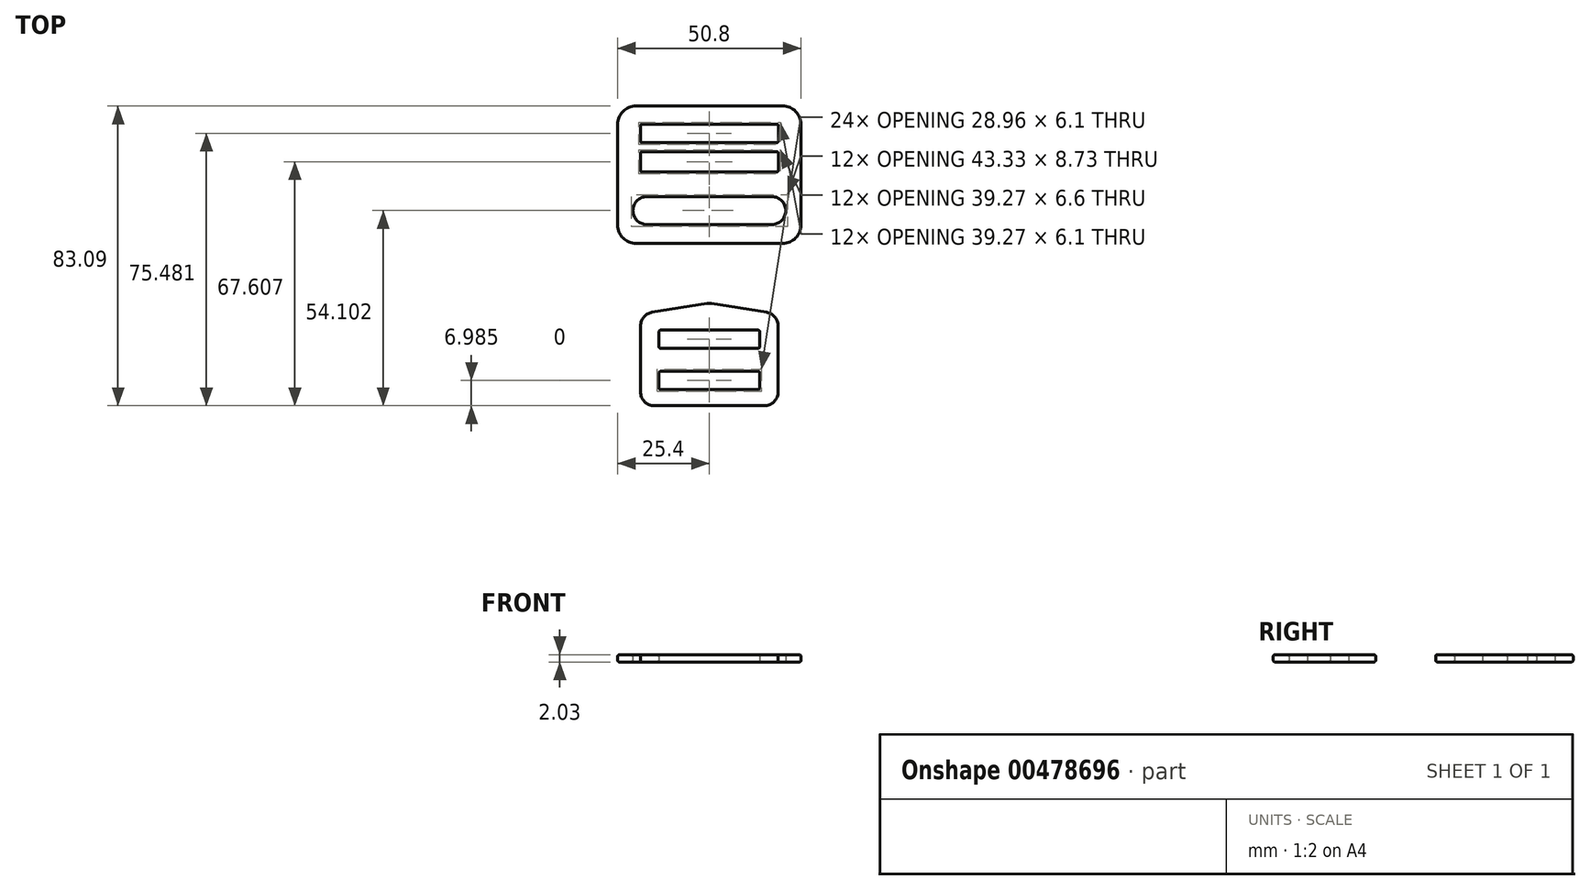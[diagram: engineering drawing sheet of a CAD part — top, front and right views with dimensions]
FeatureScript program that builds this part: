
annotation { "Feature Type Name" : "Feature", "Feature Type Description" : "" }
export const myFeature = defineFeature(function(context is Context, id is Id, definition is map)
    precondition{}
    {
        {
            var Q0;
            Q0=qCreatedBy(makeId("Top.planeOp"),FACE);
            var sketch = newSketch(context, id + "F0", { "sketchPlane" : qUnion([Q0])});
            skLineSegment(sketch, "E0.top", {"start": v(-15.24, -12.7) * mm, "end": v(15.24, -12.7) * mm});
            skLineSegment(sketch, "E0.left", {"start": v(-19.05, 9.45) * mm, "end": v(-19.05, -8.9) * mm});
            skLineSegment(sketch, "E0.right", {"start": v(19.05, 9.45) * mm, "end": v(19.05, -8.9) * mm});
            skPoint(sketch, "E1", {"position": v(0, 12.7) * mm});
            skPoint(sketch, "E2", {"position": v(19.05, 0) * mm});
            skLineSegment(sketch, "E3", {"start": v(-15.84, 13.21) * mm, "end": v(-0.6, 15.63) * mm});
            skLineSegment(sketch, "E4", {"start": v(0.6, 15.63) * mm, "end": v(15.84, 13.21) * mm});
            skPoint(sketch, "E5.visualSharp", {"position": v(-19.05, 12.7) * mm});
            skArc(sketch, "E5.filletArc", {"start": v(-15.84, 13.21) * mm, "mid": v(-18.14, 11.92) * mm, "end": v(-19.05, 9.45) * mm});
            skPoint(sketch, "E6.visualSharp", {"position": v(0, 15.73) * mm});
            skArc(sketch, "E6.filletArc", {"start": v(0.6, 15.63) * mm, "mid": v(0, 15.68) * mm, "end": v(-0.6, 15.63) * mm});
            skPoint(sketch, "E7.visualSharp", {"position": v(-19.05, -12.7) * mm});
            skArc(sketch, "E7.filletArc", {"start": v(-19.05, -8.9) * mm, "mid": v(-17.93, -11.58) * mm, "end": v(-15.24, -12.7) * mm});
            skPoint(sketch, "E8.visualSharp", {"position": v(19.05, -12.7) * mm});
            skArc(sketch, "E8.filletArc", {"start": v(15.24, -12.7) * mm, "mid": v(17.93, -11.58) * mm, "end": v(19.05, -8.9) * mm});
            skPoint(sketch, "E9.visualSharp", {"position": v(19.05, 12.7) * mm});
            skArc(sketch, "E9.filletArc", {"start": v(19.05, 9.45) * mm, "mid": v(18.14, 11.92) * mm, "end": v(15.84, 13.21) * mm});
            skSolve(sketch);
        }
        {
            var Q0;
            Q0=makeQuery(id+"F0.imprint","IMPRINT",FACE,{"disambiguationData":[TD([[makeQuery(id+"F0.imprint","IMPRINT",EDGE,{"derivedFrom":sQuery(id+"F0.wireOp",EDGE,"E0.top")}),1.0]])]});
            extrude(context, id + "F1", {"entities" : qUnion([Q0]), "depth" : 2.03 * mm});
        }
        {
            var Q0;
            Q0=qCreatedBy(makeId("Top.planeOp"),FACE);
            var sketch = newSketch(context, id + "F2", { "sketchPlane" : qUnion([Q0])});
            skLineSegment(sketch, "E10.bottom", {"start": v(-13.46, 8.26) * mm, "end": v(13.46, 8.26) * mm});
            skLineSegment(sketch, "E10.top", {"start": v(-13.46, 3.18) * mm, "end": v(13.46, 3.18) * mm});
            skLineSegment(sketch, "E10.left", {"start": v(-13.97, 7.75) * mm, "end": v(-13.97, 3.68) * mm});
            skLineSegment(sketch, "E10.right", {"start": v(13.97, 7.75) * mm, "end": v(13.97, 3.68) * mm});
            skLineSegment(sketch, "E11.bottom", {"start": v(-13.46, -8.26) * mm, "end": v(13.46, -8.26) * mm});
            skLineSegment(sketch, "E11.top", {"start": v(-13.46, -3.18) * mm, "end": v(13.46, -3.18) * mm});
            skLineSegment(sketch, "E11.left", {"start": v(-13.97, -3.68) * mm, "end": v(-13.97, -7.75) * mm});
            skLineSegment(sketch, "E11.right", {"start": v(13.97, -3.68) * mm, "end": v(13.97, -7.75) * mm});
            skPoint(sketch, "E12", {"position": v(0, 8.26) * mm});
            skPoint(sketch, "E13", {"position": v(0, -8.26) * mm});
            skLineSegment(sketch, "E14", {"start": v(-5.61, 3.17) * mm, "end": v(-5.61, -3.18) * mm, "construction": true});
            skPoint(sketch, "E15", {"position": v(-5.61, 0) * mm});
            skPoint(sketch, "E16.visualSharp", {"position": v(-13.97, 8.26) * mm});
            skArc(sketch, "E16.filletArc", {"start": v(-13.46, 8.26) * mm, "mid": v(-13.82, 8.1) * mm, "end": v(-13.97, 7.75) * mm});
            skPoint(sketch, "E17.visualSharp", {"position": v(-13.97, 3.18) * mm});
            skArc(sketch, "E17.filletArc", {"start": v(-13.97, 3.68) * mm, "mid": v(-13.82, 3.32) * mm, "end": v(-13.46, 3.18) * mm});
            skPoint(sketch, "E18.visualSharp", {"position": v(-13.97, -3.18) * mm});
            skArc(sketch, "E18.filletArc", {"start": v(-13.46, -3.18) * mm, "mid": v(-13.82, -3.32) * mm, "end": v(-13.97, -3.68) * mm});
            skPoint(sketch, "E19.visualSharp", {"position": v(13.97, 3.18) * mm});
            skArc(sketch, "E19.filletArc", {"start": v(13.46, 3.18) * mm, "mid": v(13.82, 3.32) * mm, "end": v(13.97, 3.68) * mm});
            skPoint(sketch, "E20.visualSharp", {"position": v(13.97, 8.26) * mm});
            skArc(sketch, "E20.filletArc", {"start": v(13.97, 7.75) * mm, "mid": v(13.82, 8.1) * mm, "end": v(13.46, 8.26) * mm});
            skPoint(sketch, "E21.visualSharp", {"position": v(13.97, -3.18) * mm});
            skArc(sketch, "E21.filletArc", {"start": v(13.97, -3.68) * mm, "mid": v(13.82, -3.32) * mm, "end": v(13.46, -3.17) * mm});
            skPoint(sketch, "E22.visualSharp", {"position": v(13.97, -8.26) * mm});
            skArc(sketch, "E22.filletArc", {"start": v(13.46, -8.25) * mm, "mid": v(13.82, -8.1) * mm, "end": v(13.97, -7.75) * mm});
            skPoint(sketch, "E23.visualSharp", {"position": v(-13.97, -8.26) * mm});
            skArc(sketch, "E23.filletArc", {"start": v(-13.97, -7.75) * mm, "mid": v(-13.82, -8.1) * mm, "end": v(-13.46, -8.26) * mm});
            skSolve(sketch);
        }
        {
            var Q0;
            Q0 = qSketchRegion(id + "F2", true);
            extrude(context, id + "F3", {"entities" : qUnion([Q0]), "operationType" : NewBodyOperationType.REMOVE, "oppositeDirection" : true, "depth" : -25.4 * mm});
        }
        {
            var Q0;
            Q0=makeQuery(id+"F1.opExtrude","CAP_FACE",FACE,{"disambiguationData":[OSD([sQuery(id+"F0.wireOp",EDGE,"E0.top"),sQuery(id+"F0.wireOp",EDGE,"E0.left"),sQuery(id+"F0.wireOp",EDGE,"E0.right"),sQuery(id+"F0.wireOp",EDGE,"E3"),sQuery(id+"F0.wireOp",EDGE,"E4"),sQuery(id+"F0.wireOp",EDGE,"E5.filletArc"),sQuery(id+"F0.wireOp",EDGE,"E6.filletArc"),sQuery(id+"F0.wireOp",EDGE,"E7.filletArc"),sQuery(id+"F0.wireOp",EDGE,"E8.filletArc"),sQuery(id+"F0.wireOp",EDGE,"E9.filletArc")])],"isStart":false});
            var Q1;
            Q1=makeQuery(id+"F1.opExtrude","CAP_FACE",FACE,{"disambiguationData":[OSD([sQuery(id+"F0.wireOp",EDGE,"E0.top"),sQuery(id+"F0.wireOp",EDGE,"E0.left"),sQuery(id+"F0.wireOp",EDGE,"E0.right"),sQuery(id+"F0.wireOp",EDGE,"E3"),sQuery(id+"F0.wireOp",EDGE,"E4"),sQuery(id+"F0.wireOp",EDGE,"E5.filletArc"),sQuery(id+"F0.wireOp",EDGE,"E6.filletArc"),sQuery(id+"F0.wireOp",EDGE,"E7.filletArc"),sQuery(id+"F0.wireOp",EDGE,"E8.filletArc"),sQuery(id+"F0.wireOp",EDGE,"E9.filletArc")])],"isStart":true});
            fillet(context, id + "F4", {"entities" : qUnion([Q0, Q1]), "radius" : 0.5 * mm, "tangentPropagation" : true, "allowEdgeOverflow" : false});
        }
        {
            var Q0;
            Q0=qCreatedBy(makeId("Top.planeOp"),FACE);
            var sketch = newSketch(context, id + "F5", { "sketchPlane" : qUnion([Q0])});
            skLineSegment(sketch, "E24.bottom", {"start": v(-20.32, 32.3) * mm, "end": v(20.32, 32.3) * mm});
            skLineSegment(sketch, "E24.top", {"start": v(-20.32, 70.4) * mm, "end": v(20.32, 70.4) * mm});
            skLineSegment(sketch, "E24.left", {"start": v(-25.4, 37.37) * mm, "end": v(-25.4, 65.31) * mm});
            skLineSegment(sketch, "E24.right", {"start": v(25.4, 37.37) * mm, "end": v(25.4, 65.31) * mm});
            skPoint(sketch, "E25", {"position": v(0, 32.3) * mm});
            skPoint(sketch, "E26.visualSharp", {"position": v(-25.4, 70.4) * mm});
            skArc(sketch, "E26.filletArc", {"start": v(-20.32, 70.4) * mm, "mid": v(-23.91, 68.9) * mm, "end": v(-25.4, 65.31) * mm});
            skPoint(sketch, "E27.visualSharp", {"position": v(25.4, 70.4) * mm});
            skArc(sketch, "E27.filletArc", {"start": v(25.4, 65.31) * mm, "mid": v(23.91, 68.9) * mm, "end": v(20.32, 70.4) * mm});
            skPoint(sketch, "E28.visualSharp", {"position": v(-25.4, 32.3) * mm});
            skArc(sketch, "E28.filletArc", {"start": v(-25.4, 37.37) * mm, "mid": v(-23.91, 33.78) * mm, "end": v(-20.32, 32.3) * mm});
            skPoint(sketch, "E29.visualSharp", {"position": v(25.4, 32.3) * mm});
            skArc(sketch, "E29.filletArc", {"start": v(20.32, 32.3) * mm, "mid": v(23.91, 33.78) * mm, "end": v(25.4, 37.37) * mm});
            skSolve(sketch);
        }
        {
            var Q0;
            Q0 = qSketchRegion(id + "F5", true);
            extrude(context, id + "F6", {"entities" : qUnion([Q0]), "depth" : 2.03 * mm});
        }
        {
            var Q0;
            Q0=qCreatedBy(makeId("Top.planeOp"),FACE);
            var sketch = newSketch(context, id + "F7", { "sketchPlane" : qUnion([Q0])});
            skLineSegment(sketch, "E30.bottom", {"start": v(-18.62, 65.32) * mm, "end": v(18.62, 65.32) * mm});
            skLineSegment(sketch, "E30.top", {"start": v(-18.62, 60.24) * mm, "end": v(18.62, 60.24) * mm});
            skLineSegment(sketch, "E30.left", {"start": v(-19.13, 64.81) * mm, "end": v(-19.13, 60.75) * mm});
            skLineSegment(sketch, "E30.right", {"start": v(19.13, 64.81) * mm, "end": v(19.13, 60.75) * mm});
            skPoint(sketch, "E31", {"position": v(0, 60.24) * mm});
            skLineSegment(sketch, "E32.bottom", {"start": v(-18.62, 57.7) * mm, "end": v(18.62, 57.7) * mm});
            skLineSegment(sketch, "E32.top", {"start": v(-18.62, 52.11) * mm, "end": v(18.62, 52.11) * mm});
            skLineSegment(sketch, "E32.left", {"start": v(-19.13, 57.2) * mm, "end": v(-19.13, 52.62) * mm});
            skLineSegment(sketch, "E32.right", {"start": v(19.13, 57.2) * mm, "end": v(19.13, 52.62) * mm});
            skPoint(sketch, "E33", {"position": v(0, 52.11) * mm});
            skLineSegment(sketch, "E34.bottom", {"start": v(-17.35, 37.55) * mm, "end": v(17.35, 37.55) * mm});
            skLineSegment(sketch, "E34.top", {"start": v(-17.35, 45.26) * mm, "end": v(17.35, 45.26) * mm});
            skLineSegment(sketch, "E34.left", {"start": v(-21.16, 41.36) * mm, "end": v(-21.16, 41.45) * mm});
            skLineSegment(sketch, "E34.right", {"start": v(21.16, 41.36) * mm, "end": v(21.16, 41.45) * mm});
            skPoint(sketch, "E35", {"position": v(0, 45.26) * mm});
            skPoint(sketch, "E36.visualSharp", {"position": v(-21.16, 45.26) * mm});
            skArc(sketch, "E36.filletArc", {"start": v(-17.35, 45.26) * mm, "mid": v(-20.04, 44.14) * mm, "end": v(-21.16, 41.45) * mm});
            skPoint(sketch, "E37.visualSharp", {"position": v(-21.16, 37.55) * mm});
            skArc(sketch, "E37.filletArc", {"start": v(-21.16, 41.36) * mm, "mid": v(-20.04, 38.66) * mm, "end": v(-17.35, 37.55) * mm});
            skPoint(sketch, "E38.visualSharp", {"position": v(21.16, 37.55) * mm});
            skArc(sketch, "E38.filletArc", {"start": v(17.35, 37.55) * mm, "mid": v(20.04, 38.66) * mm, "end": v(21.16, 41.36) * mm});
            skPoint(sketch, "E39.visualSharp", {"position": v(21.16, 45.26) * mm});
            skArc(sketch, "E39.filletArc", {"start": v(21.16, 41.45) * mm, "mid": v(20.04, 44.14) * mm, "end": v(17.35, 45.26) * mm});
            skPoint(sketch, "E40.visualSharp", {"position": v(-19.13, 65.32) * mm});
            skArc(sketch, "E40.filletArc", {"start": v(-18.62, 65.32) * mm, "mid": v(-18.98, 65.17) * mm, "end": v(-19.13, 64.81) * mm});
            skPoint(sketch, "E41.visualSharp", {"position": v(-19.13, 60.24) * mm});
            skArc(sketch, "E41.filletArc", {"start": v(-19.13, 60.75) * mm, "mid": v(-18.98, 60.4) * mm, "end": v(-18.62, 60.24) * mm});
            skPoint(sketch, "E42.visualSharp", {"position": v(19.13, 60.24) * mm});
            skArc(sketch, "E42.filletArc", {"start": v(18.62, 60.24) * mm, "mid": v(18.98, 60.4) * mm, "end": v(19.13, 60.75) * mm});
            skPoint(sketch, "E43.visualSharp", {"position": v(19.13, 57.7) * mm});
            skArc(sketch, "E43.filletArc", {"start": v(19.13, 57.2) * mm, "mid": v(18.98, 57.55) * mm, "end": v(18.62, 57.7) * mm});
            skPoint(sketch, "E44.visualSharp", {"position": v(19.13, 52.11) * mm});
            skArc(sketch, "E44.filletArc", {"start": v(18.62, 52.11) * mm, "mid": v(18.98, 52.26) * mm, "end": v(19.13, 52.62) * mm});
            skPoint(sketch, "E45.visualSharp", {"position": v(-19.13, 52.11) * mm});
            skArc(sketch, "E45.filletArc", {"start": v(-19.13, 52.62) * mm, "mid": v(-18.98, 52.26) * mm, "end": v(-18.62, 52.11) * mm});
            skPoint(sketch, "E46.visualSharp", {"position": v(-19.13, 57.7) * mm});
            skArc(sketch, "E46.filletArc", {"start": v(-18.62, 57.7) * mm, "mid": v(-18.98, 57.55) * mm, "end": v(-19.13, 57.2) * mm});
            skPoint(sketch, "E47.visualSharp", {"position": v(19.13, 65.32) * mm});
            skArc(sketch, "E47.filletArc", {"start": v(19.13, 64.81) * mm, "mid": v(18.98, 65.17) * mm, "end": v(18.62, 65.32) * mm});
            skSolve(sketch);
        }
        {
            var Q0;
            Q0 = qSketchRegion(id + "F7", true);
            extrude(context, id + "F8", {"entities" : qUnion([Q0]), "operationType" : NewBodyOperationType.REMOVE, "depth" : 14.96 * mm});
        }
        {
            var Q0;
            Q0=makeQuery(id+"F6.opExtrude","CAP_FACE",FACE,{"disambiguationData":[OSD([sQuery(id+"F5.wireOp",EDGE,"E24.bottom"),sQuery(id+"F5.wireOp",EDGE,"E24.top"),sQuery(id+"F5.wireOp",EDGE,"E24.left"),sQuery(id+"F5.wireOp",EDGE,"E24.right"),sQuery(id+"F5.wireOp",EDGE,"E26.filletArc"),sQuery(id+"F5.wireOp",EDGE,"E27.filletArc"),sQuery(id+"F5.wireOp",EDGE,"E28.filletArc"),sQuery(id+"F5.wireOp",EDGE,"E29.filletArc")])],"isStart":true});
            var Q1;
            Q1=makeQuery(id+"F6.opExtrude","CAP_FACE",FACE,{"disambiguationData":[OSD([sQuery(id+"F5.wireOp",EDGE,"E24.bottom"),sQuery(id+"F5.wireOp",EDGE,"E24.top"),sQuery(id+"F5.wireOp",EDGE,"E24.left"),sQuery(id+"F5.wireOp",EDGE,"E24.right"),sQuery(id+"F5.wireOp",EDGE,"E26.filletArc"),sQuery(id+"F5.wireOp",EDGE,"E27.filletArc"),sQuery(id+"F5.wireOp",EDGE,"E28.filletArc"),sQuery(id+"F5.wireOp",EDGE,"E29.filletArc")])],"isStart":false});
            fillet(context, id + "F9", {"entities" : qUnion([Q0, Q1]), "radius" : 0.5 * mm, "tangentPropagation" : true, "allowEdgeOverflow" : false});
        }
    });
